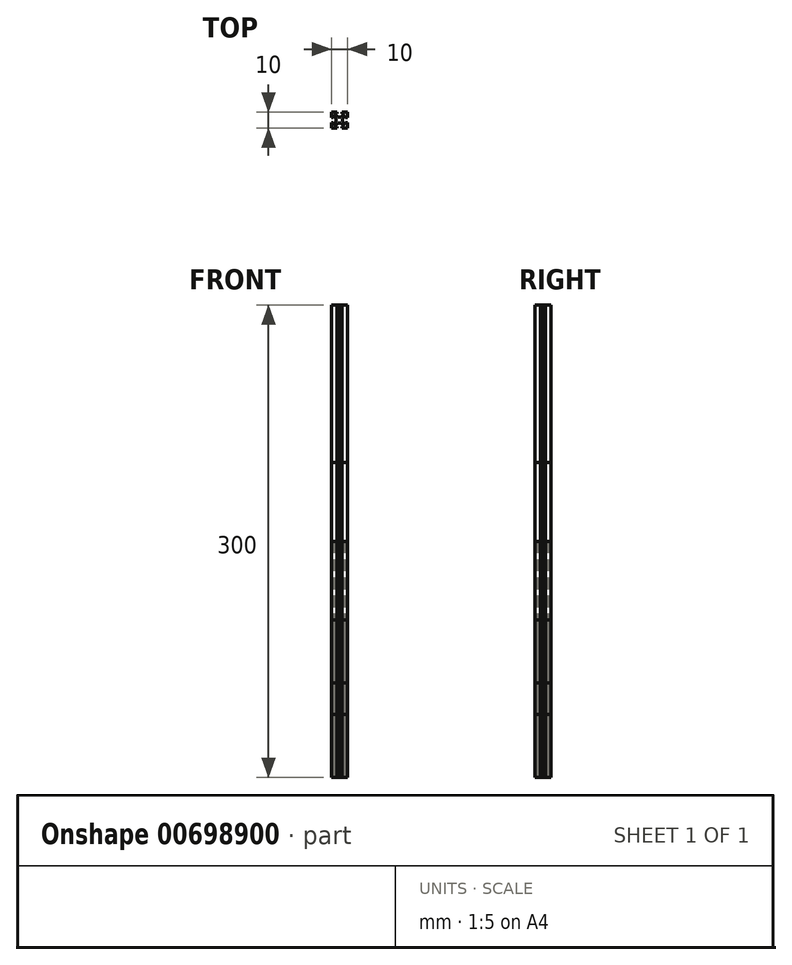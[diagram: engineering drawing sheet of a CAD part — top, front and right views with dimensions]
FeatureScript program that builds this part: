
annotation { "Feature Type Name" : "Feature", "Feature Type Description" : "" }
export const myFeature = defineFeature(function(context is Context, id is Id, definition is map)
    precondition{}
    {
        {
            var Q0;
            Q0=qCreatedBy(makeId("Top.planeOp"),FACE);
            var sketch = newSketch(context, id + "F0", { "sketchPlane" : qUnion([Q0])});
            skPoint(sketch, "E0.rect.middle", {"position": v(0, 0) * mm});
            skLineSegment(sketch, "E1.MirrorCS", {"start": v(1.5, -4) * mm, "end": v(1.5, -5) * mm});
            skLineSegment(sketch, "E2.MirrorCS", {"start": v(-1.5, -4) * mm, "end": v(-1.5, -5) * mm});
            skLineSegment(sketch, "E3.rect.top", {"start": v(5, -5) * mm, "end": v(-5, -5) * mm});
            skLineSegment(sketch, "E3.rect.left", {"start": v(5, 5) * mm, "end": v(5, -5) * mm});
            skLineSegment(sketch, "E3.rect.right", {"start": v(-5, 5) * mm, "end": v(-5, -5) * mm});
            skLineSegment(sketch, "E4.MirrorCS", {"start": v(-3, -4) * mm, "end": v(-1.5, -4) * mm});
            skLineSegment(sketch, "E5", {"start": v(0, 5) * mm, "end": v(0, -5) * mm, "construction": true});
            skLineSegment(sketch, "E3.rect.bottom", {"start": v(5, 5) * mm, "end": v(-5, 5) * mm});
            skLineSegment(sketch, "E6.MirrorCS", {"start": v(3, -4) * mm, "end": v(1.5, -4) * mm});
            skLineSegment(sketch, "E7", {"start": v(1.5, 4) * mm, "end": v(1.5, 5) * mm});
            skLineSegment(sketch, "E8.MirrorCS", {"start": v(4, -3) * mm, "end": v(4, -1.5) * mm});
            skLineSegment(sketch, "E9.MirrorCS", {"start": v(-2, -1) * mm, "end": v(-4, -3) * mm});
            skLineSegment(sketch, "E10.MirrorCS", {"start": v(0, -2) * mm, "end": v(-1, -2) * mm});
            skLineSegment(sketch, "E11.MirrorCS", {"start": v(-1, -2) * mm, "end": v(-3, -4) * mm});
            skLineSegment(sketch, "E12.MirrorCS", {"start": v(-1.5, 4) * mm, "end": v(-1.5, 5) * mm});
            skLineSegment(sketch, "E13.MirrorCS", {"start": v(1, -2) * mm, "end": v(3, -4) * mm});
            skLineSegment(sketch, "E14.MirrorCS", {"start": v(-3, 4) * mm, "end": v(-1.5, 4) * mm});
            skLineSegment(sketch, "E15", {"start": v(0, 0) * mm, "end": v(5, 5) * mm, "construction": true});
            skLineSegment(sketch, "E16", {"start": v(3, 4) * mm, "end": v(1.5, 4) * mm});
            skLineSegment(sketch, "E17.MirrorCS", {"start": v(-1, 2) * mm, "end": v(-3, 4) * mm});
            skLineSegment(sketch, "E18.MirrorCS", {"start": v(2, -1) * mm, "end": v(4, -3) * mm});
            skLineSegment(sketch, "E19.MirrorCS", {"start": v(0, -2) * mm, "end": v(1, -2) * mm});
            skLineSegment(sketch, "E20.MirrorCS", {"start": v(-4, -3) * mm, "end": v(-4, -1.5) * mm});
            skLineSegment(sketch, "E21.MirrorCS", {"start": v(-4, -1.5) * mm, "end": v(-5, -1.5) * mm});
            skLineSegment(sketch, "E22.MirrorCS", {"start": v(4, -1.5) * mm, "end": v(5, -1.5) * mm});
            skLineSegment(sketch, "E23.MirrorCS", {"start": v(4, 3) * mm, "end": v(4, 1.5) * mm});
            skLineSegment(sketch, "E24", {"start": v(0, 2) * mm, "end": v(1, 2) * mm});
            skLineSegment(sketch, "E25.MirrorCS", {"start": v(-2, 0) * mm, "end": v(-2, -1) * mm});
            skLineSegment(sketch, "E26", {"start": v(1, 2) * mm, "end": v(3, 4) * mm});
            skLineSegment(sketch, "E27.MirrorCS", {"start": v(0, 2) * mm, "end": v(-1, 2) * mm});
            skLineSegment(sketch, "E28.MirrorCS", {"start": v(-4, 3) * mm, "end": v(-4, 1.5) * mm});
            skLineSegment(sketch, "E29.MirrorCS", {"start": v(2, 1) * mm, "end": v(4, 3) * mm});
            skLineSegment(sketch, "E30.MirrorCS", {"start": v(2, 0) * mm, "end": v(2, -1) * mm});
            skLineSegment(sketch, "E31.MirrorCS", {"start": v(2, 0) * mm, "end": v(2, 1) * mm});
            skLineSegment(sketch, "E32.MirrorCS", {"start": v(4, 1.5) * mm, "end": v(5, 1.5) * mm});
            skLineSegment(sketch, "E33", {"start": v(-5, 0) * mm, "end": v(5, 0) * mm, "construction": true});
            skLineSegment(sketch, "E34.MirrorCS", {"start": v(-2, 1) * mm, "end": v(-4, 3) * mm});
            skLineSegment(sketch, "E35.MirrorCS", {"start": v(-4, 1.5) * mm, "end": v(-5, 1.5) * mm});
            skLineSegment(sketch, "E36.MirrorCS", {"start": v(-2, 0) * mm, "end": v(-2, 1) * mm});
            skSolve(sketch);
        }
        {
            var Q0;
            {var subQ8=sQuery(id+"F0.wireOp",EDGE,"E1.MirrorCS");Q0=makeQuery(id+"F0.imprint","IMPRINT",FACE,{"disambiguationData":[TD([[makeQuery(id+"F0.imprint","IMPRINT",EDGE,{"derivedFrom":subQ8}),1.0]])]});}
            extrude(context, id + "F1", {"entities" : qUnion([Q0]), "depth" : 200 * mm});
        }
        {
            var Q0;
            {var subQ8=sQuery(id+"F0.wireOp",EDGE,"E1.MirrorCS");Q0=makeQuery(id+"F0.imprint","IMPRINT",FACE,{"disambiguationData":[TD([[makeQuery(id+"F0.imprint","IMPRINT",EDGE,{"derivedFrom":subQ8}),1.0]])]});}
            extrude(context, id + "F2", {"entities" : qUnion([Q0]), "depth" : 150 * mm});
        }
        {
            var Q0;
            {var subQ8=sQuery(id+"F0.wireOp",EDGE,"E1.MirrorCS");Q0=makeQuery(id+"F0.imprint","IMPRINT",FACE,{"disambiguationData":[TD([[makeQuery(id+"F0.imprint","IMPRINT",EDGE,{"derivedFrom":subQ8}),1.0]])]});}
            extrude(context, id + "F3", {"entities" : qUnion([Q0]), "depth" : 100 * mm});
        }
        {
            var Q0;
            {var subQ8=sQuery(id+"F0.wireOp",EDGE,"E1.MirrorCS");Q0=makeQuery(id+"F0.imprint","IMPRINT",FACE,{"disambiguationData":[TD([[makeQuery(id+"F0.imprint","IMPRINT",EDGE,{"derivedFrom":subQ8}),1.0]])]});}
            extrude(context, id + "F4", {"entities" : qUnion([Q0]), "depth" : 300 * mm});
        }
        {
            var Q0;
            {var subQ8=sQuery(id+"F0.wireOp",EDGE,"E1.MirrorCS");Q0=makeQuery(id+"F0.imprint","IMPRINT",FACE,{"disambiguationData":[TD([[makeQuery(id+"F0.imprint","IMPRINT",EDGE,{"derivedFrom":subQ8}),1.0]])]});}
            extrude(context, id + "F5", {"entities" : qUnion([Q0]), "depth" : 60 * mm});
        }
        {
            var Q0;
            {var subQ8=sQuery(id+"F0.wireOp",EDGE,"E1.MirrorCS");Q0=makeQuery(id+"F0.imprint","IMPRINT",FACE,{"disambiguationData":[TD([[makeQuery(id+"F0.imprint","IMPRINT",EDGE,{"derivedFrom":subQ8}),1.0]])]});}
            extrude(context, id + "F6", {"entities" : qUnion([Q0]), "depth" : 40 * mm});
        }
    });
